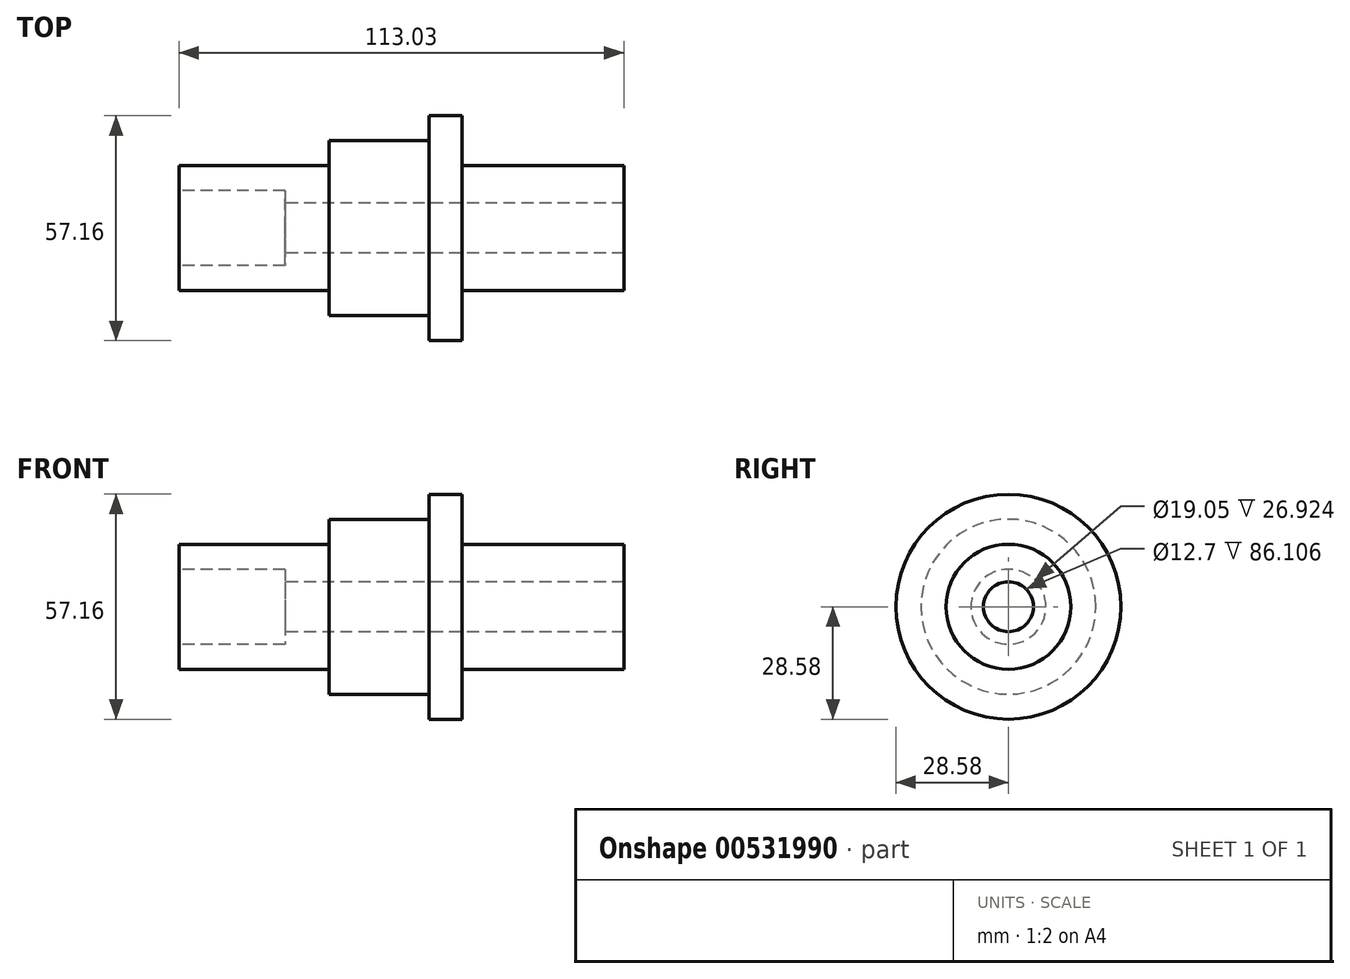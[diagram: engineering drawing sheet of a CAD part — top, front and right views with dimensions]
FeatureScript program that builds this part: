
annotation { "Feature Type Name" : "Feature", "Feature Type Description" : "" }
export const myFeature = defineFeature(function(context is Context, id is Id, definition is map)
    precondition{}
    {
        {
            var Q0;
            Q0=qCreatedBy(makeId("Front.planeOp"),FACE);
            var sketch = newSketch(context, id + "F0", { "sketchPlane" : qUnion([Q0])});
            skLineSegment(sketch, "E0", {"start": v(-106.45, 0) * mm, "end": v(106.45, 0) * mm, "construction": true});
            skPoint(sketch, "E1", {"position": v(0, 0) * mm});
            skLineSegment(sketch, "E2.bottom", {"start": v(0, 15.88) * mm, "end": v(41.15, 15.88) * mm});
            skLineSegment(sketch, "E2.top", {"start": v(-44.96, 6.35) * mm, "end": v(41.15, 6.35) * mm});
            skLineSegment(sketch, "E2.right", {"start": v(41.15, 15.88) * mm, "end": v(41.15, 6.35) * mm});
            skLineSegment(sketch, "E3.top", {"start": v(0, 28.58) * mm, "end": v(-8.38, 28.58) * mm});
            skLineSegment(sketch, "E4.top", {"start": v(-8.38, 22.23) * mm, "end": v(-33.78, 22.22) * mm});
            skLineSegment(sketch, "E4.right", {"start": v(-33.78, 15.88) * mm, "end": v(-33.78, 22.22) * mm});
            skLineSegment(sketch, "E5.bottom", {"start": v(-44.96, 9.53) * mm, "end": v(-71.88, 9.53) * mm});
            skLineSegment(sketch, "E5.top", {"start": v(-33.78, 15.88) * mm, "end": v(-71.88, 15.87) * mm});
            skLineSegment(sketch, "E5.right", {"start": v(-71.88, 9.53) * mm, "end": v(-71.88, 15.87) * mm});
            skLineSegment(sketch, "E6", {"start": v(0, 28.58) * mm, "end": v(0, 15.88) * mm});
            skLineSegment(sketch, "E7", {"start": v(-8.38, 28.58) * mm, "end": v(-8.38, 22.23) * mm});
            skLineSegment(sketch, "E8", {"start": v(-44.96, 9.53) * mm, "end": v(-44.96, 6.35) * mm});
            skSolve(sketch);
        }
        {
            var Q0;
            Q0=makeQuery(id+"F0.imprint","IMPRINT",FACE,{"disambiguationData":[TD([[makeQuery(id+"F0.imprint","IMPRINT",EDGE,{"derivedFrom":sQuery(id+"F0.wireOp",EDGE,"E2.bottom")}),-1.0]])]});
            var Q1;
            Q1=sQuery(id+"F0.wireOp",EDGE,"E0");
            revolve(context, id + "F1", {"entities" : qUnion([Q0]), "axis" : qUnion([Q1]), "revolveType" : RevolveType.FULL});
        }
    });
